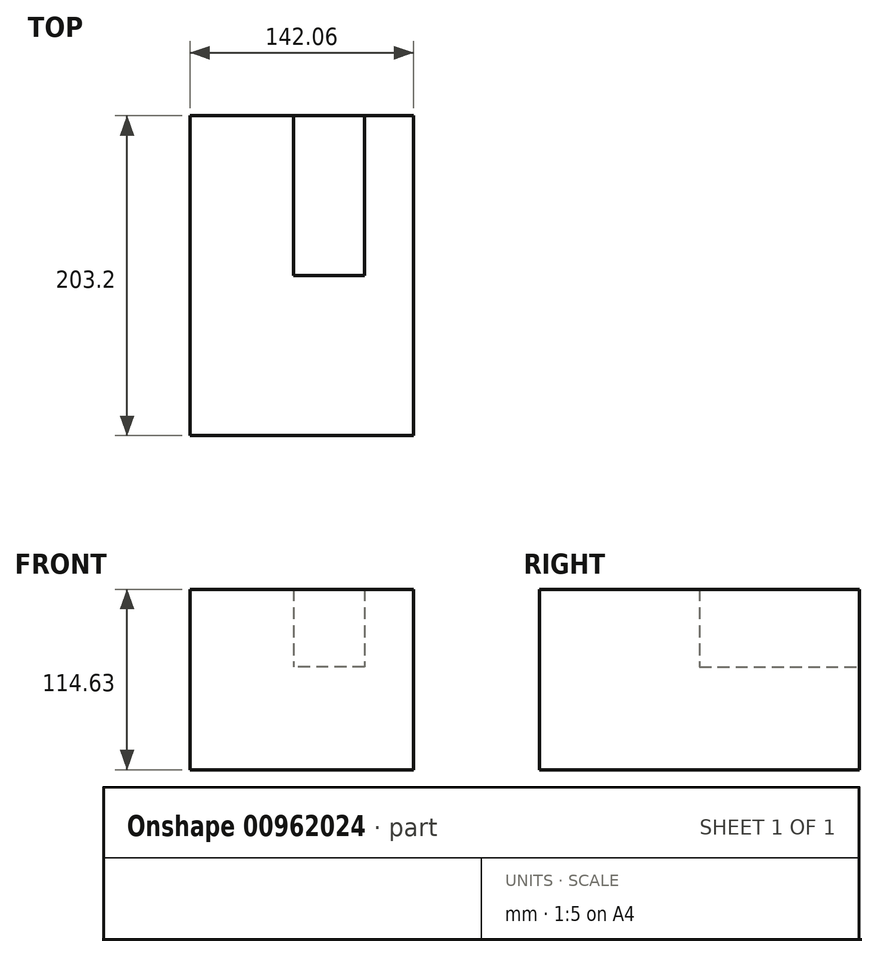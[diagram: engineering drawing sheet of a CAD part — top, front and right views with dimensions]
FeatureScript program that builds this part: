
annotation { "Feature Type Name" : "Feature", "Feature Type Description" : "" }
export const myFeature = defineFeature(function(context is Context, id is Id, definition is map)
    precondition{}
    {
        {
            var Q0;
            Q0=qCreatedBy(makeId("Front.planeOp"),FACE);
            var sketch = newSketch(context, id + "F0", { "sketchPlane" : qUnion([Q0])});
            skLineSegment(sketch, "E0.bottom", {"start": v(71.03, 19.98) * mm, "end": v(-71.03, 19.98) * mm});
            skLineSegment(sketch, "E0.top", {"start": v(71.03, -19.98) * mm, "end": v(-71.03, -19.98) * mm});
            skLineSegment(sketch, "E0.left", {"start": v(71.03, 19.98) * mm, "end": v(71.03, -19.98) * mm});
            skLineSegment(sketch, "E0.right", {"start": v(-71.03, 19.98) * mm, "end": v(-71.03, -19.98) * mm});
            skPoint(sketch, "E0.middle", {"position": v(0, 0) * mm});
            skSolve(sketch);
        }
        {
            var Q0;
            Q0 = qSketchRegion(id + "F0", true);
            extrude(context, id + "F1", {"entities" : qUnion([Q0]), "depth" : 203.2 * mm, "offsetDistance" : 25.4 * mm});
        }
        {
            var Q0;
            Q0=makeQuery(id+"F1.opExtrude","SWEPT_FACE",FACE,{"disambiguationData":[OSD([sQuery(id+"F0.wireOp",EDGE,"E0.bottom")])]});
            var sketch = newSketch(context, id + "F2", { "sketchPlane" : qUnion([Q0])});
            skLineSegment(sketch, "E1.bottom", {"start": v(39.78, -101.6) * mm, "end": v(-5.14, -101.6) * mm});
            skLineSegment(sketch, "E1.top", {"start": v(39.78, 41) * mm, "end": v(-5.14, 41) * mm});
            skLineSegment(sketch, "E1.left", {"start": v(39.78, -101.6) * mm, "end": v(39.78, 41) * mm});
            skLineSegment(sketch, "E1.right", {"start": v(-5.14, -101.6) * mm, "end": v(-5.14, 41) * mm});
            skPoint(sketch, "E1.middle", {"position": v(17.32, -30.3) * mm});
            skPoint(sketch, "E1.cornerSnap0", {"position": v(71.03, -101.6) * mm});
            skSolve(sketch);
        }
        {
            var Q0;
            {var subQ0=sQuery(id+"F2.wireOp",EDGE,"E1.bottom");Q0=makeQuery(id+"F2.imprint","IMPRINT",FACE,{"disambiguationData":[TD([[makeQuery(id+"F2.imprint","IMPRINT",EDGE,{"derivedFrom":subQ0}),-1.0]])]});}
            extrude(context, id + "F3", {"entities" : qUnion([Q0]), "operationType" : NewBodyOperationType.ADD, "depth" : 25.4 * mm, "offsetDistance" : 25.4 * mm});
        }
        {
            var Q0;
            Q0=makeQuery(id+"F1.opExtrude","SWEPT_FACE",FACE,{"disambiguationData":[OSD([sQuery(id+"F0.wireOp",EDGE,"E0.bottom")])]});
            extrude(context, id + "F4", {"entities" : qUnion([Q0]), "operationType" : NewBodyOperationType.ADD, "depth" : 74.68 * mm, "offsetDistance" : 25.4 * mm});
        }
        {
            var Q0;
            Q0=makeQuery(id+"F4.opExtrude","SWEPT_FACE",FACE,{"disambiguationData":[OSD([sQuery(id+"F2.wireOp",EDGE,"E1.bottom")])]});
            extrude(context, id + "F5", {"entities" : qUnion([Q0]), "operationType" : NewBodyOperationType.ADD, "oppositeDirection" : true, "depth" : 73.9 * mm, "offsetDistance" : 25.4 * mm});
        }
        {
            var Q0;
            Q0=makeQuery(id+"F4.opExtrude","SWEPT_FACE",FACE,{"disambiguationData":[OSD([sQuery(id+"F2.wireOp",EDGE,"E1.bottom")])]});
            extrude(context, id + "F6", {"entities" : qUnion([Q0]), "operationType" : NewBodyOperationType.ADD, "oppositeDirection" : true, "depth" : 64 * mm, "offsetDistance" : 25.4 * mm});
        }
        {
            var Q0;
            Q0=makeQuery(id+"F3.opExtrude","CAP_FACE",FACE,{"disambiguationData":[OSD([sQuery(id+"F0.wireOp",EDGE,"E0.bottom"),sQuery(id+"F2.wireOp",EDGE,"E1.bottom"),sQuery(id+"F2.wireOp",EDGE,"E1.left"),sQuery(id+"F2.wireOp",EDGE,"E1.right")])],"isStart":false});
            extrude(context, id + "F7", {"entities" : qUnion([Q0]), "operationType" : NewBodyOperationType.ADD, "oppositeDirection" : true, "depth" : 17.53 * mm, "offsetDistance" : 25.4 * mm});
        }
        {
            var Q0;
            Q0=makeQuery(id+"F4.opExtrude","CAP_FACE",FACE,{"disambiguationData":[OSD([sQuery(id+"F0.wireOp",EDGE,"E0.bottom")])],"isStart":false});
            var sketch = newSketch(context, id + "F8", { "sketchPlane" : qUnion([Q0])});
            skCircle(sketch, "E2", {"center": v(-25.04, -175.1) * mm, "radius": 12.97 * mm});
            skSolve(sketch);
        }
        {
            var Q0;
            Q0=makeQuery(id+"F8.imprint","IMPRINT",FACE,{"disambiguationData":[TD([[makeQuery(id+"F8.imprint","IMPRINT",EDGE,{"derivedFrom":sQuery(id+"F8.wireOp",EDGE,"E2")}),1.0]])]});
            extrude(context, id + "F9", {"entities" : qUnion([Q0]), "operationType" : NewBodyOperationType.ADD, "oppositeDirection" : true, "depth" : 96.01 * mm, "offsetDistance" : 25.4 * mm});
        }
    });
